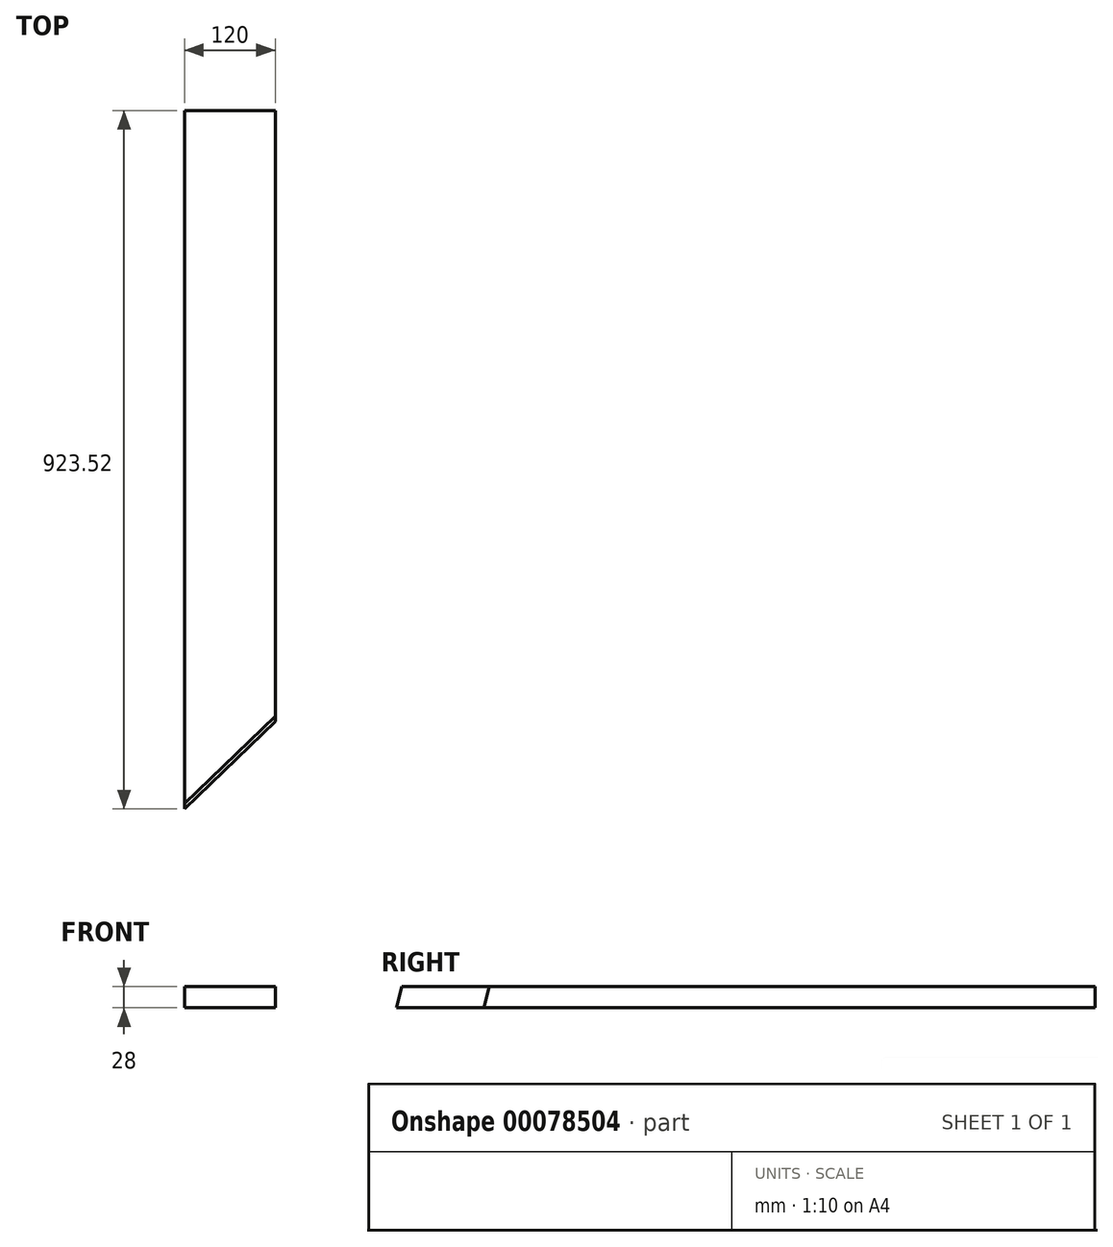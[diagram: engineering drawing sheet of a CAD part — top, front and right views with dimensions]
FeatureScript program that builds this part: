
annotation { "Feature Type Name" : "Feature", "Feature Type Description" : "" }
export const myFeature = defineFeature(function(context is Context, id is Id, definition is map)
    precondition{}
    {
        {
            var Q0;
            Q0=qCreatedBy(makeId("Front.planeOp"),FACE);
            var sketch = newSketch(context, id + "F0", { "sketchPlane" : qUnion([Q0])});
            skLineSegment(sketch, "E0.bottom", {"start": v(60, -14) * mm, "end": v(-60, -14) * mm});
            skLineSegment(sketch, "E0.top", {"start": v(60, 14) * mm, "end": v(-60, 14) * mm});
            skLineSegment(sketch, "E0.left", {"start": v(60, -14) * mm, "end": v(60, 14) * mm});
            skLineSegment(sketch, "E0.right", {"start": v(-60, -14) * mm, "end": v(-60, 14) * mm});
            skPoint(sketch, "E0.middle", {"position": v(0, 0) * mm});
            skSolve(sketch);
        }
        {
            var Q0;
            Q0=makeQuery(id+"F0.imprint","IMPRINT",FACE,{"disambiguationData":[TD([[makeQuery(id+"F0.imprint","IMPRINT",EDGE,{"derivedFrom":sQuery(id+"F0.wireOp",EDGE,"E0.bottom")}),-1.0]])]});
            extrude(context, id + "F1", {"entities" : qUnion([Q0]), "endBound" : BoundingType.SYMMETRIC, "depth" : 925 * mm});
        }
        {
            var Q0;
            Q0=makeQuery(id+"F1.opExtrude","CAP_EDGE",EDGE,{"disambiguationData":[OSD([sQuery(id+"F0.wireOp",EDGE,"E0.left")])],"isStart":false});
            chamfer(context, id + "F2", {"entities" : qUnion([Q0]), "chamferType" : ChamferType.OFFSET_ANGLE, "width" : 120 * mm, "oppositeDirection" : false, "angle" : 44 * degree, "tangentPropagation" : true});
        }
        {
            var Q0;
            Q0=makeQuery(id+"F2.opChamfer","BLEND_EDGE",EDGE,{"blendedFrom":[makeQuery(id+"F1.opExtrude","CAP_EDGE",EDGE,{"disambiguationData":[OSD([sQuery(id+"F0.wireOp",EDGE,"E0.left")])],"isStart":false}),makeQuery(id+"F1.opExtrude","SWEPT_FACE",FACE,{"disambiguationData":[OSD([sQuery(id+"F0.wireOp",EDGE,"E0.top")])]})],"blendedInto":[makeQuery(id+"F1.opExtrude","SWEPT_FACE",FACE,{"disambiguationData":[OSD([sQuery(id+"F0.wireOp",EDGE,"E0.top")])]})]});
            chamfer(context, id + "F3", {"entities" : qUnion([Q0]), "chamferType" : ChamferType.OFFSET_ANGLE, "width" : 6 * mm, "oppositeDirection" : false, "angle" : 80 * degree, "tangentPropagation" : true});
        }
    });
